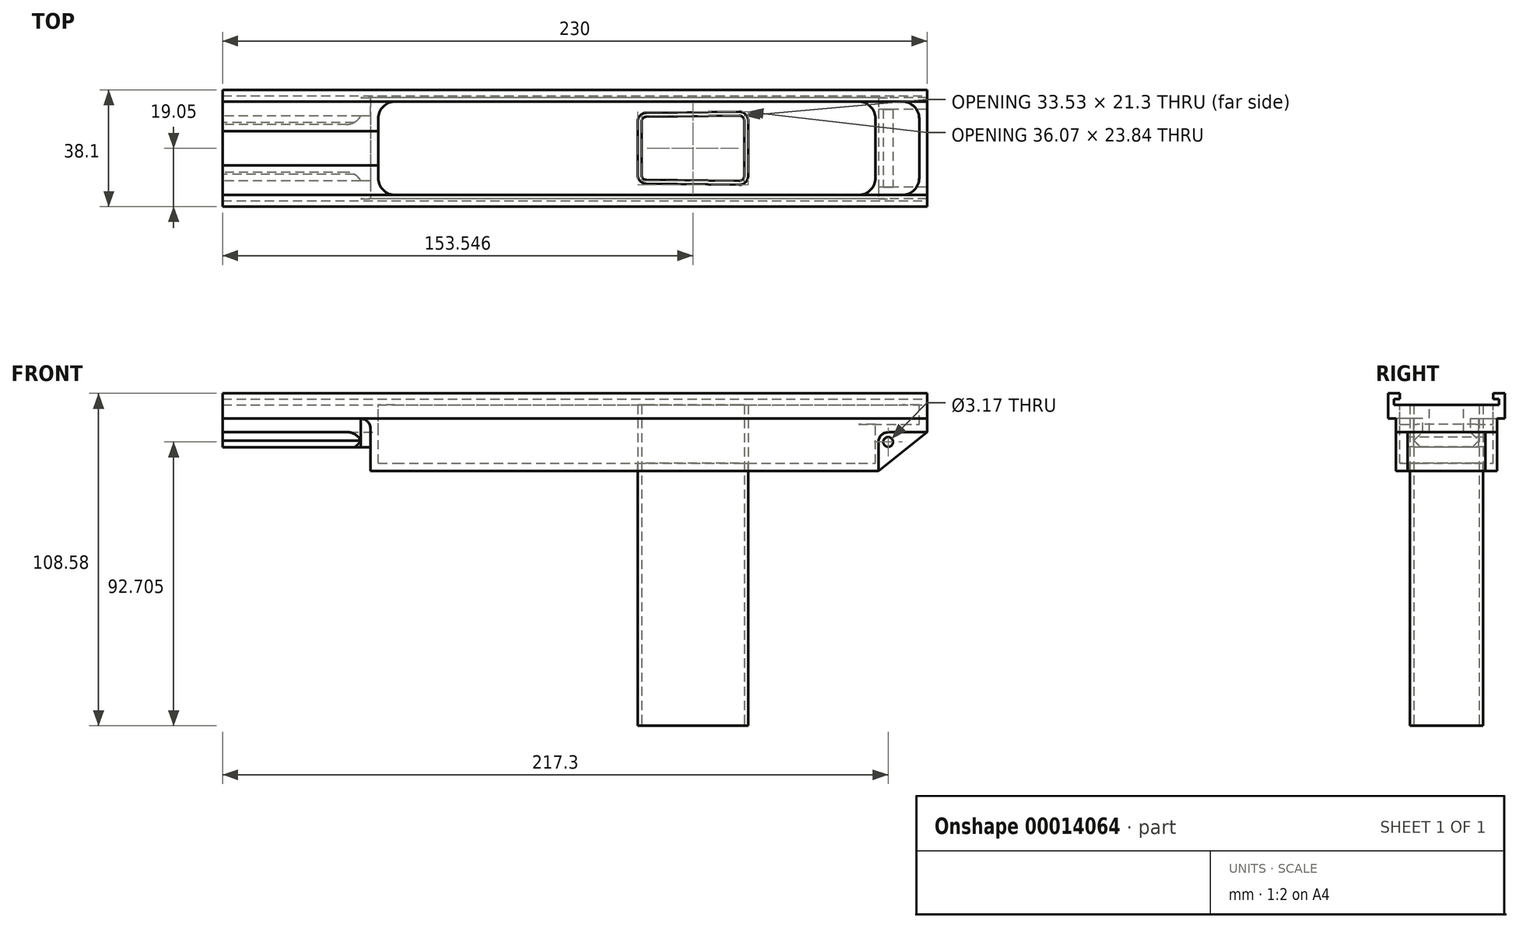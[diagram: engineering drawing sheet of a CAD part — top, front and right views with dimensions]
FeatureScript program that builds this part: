
annotation { "Feature Type Name" : "Feature", "Feature Type Description" : "" }
export const myFeature = defineFeature(function(context is Context, id is Id, definition is map)
    precondition{}
    {
        {
            var Q0;
            Q0=qCreatedBy(makeId("Top.planeOp"),FACE);
            var sketch = newSketch(context, id + "F0", { "sketchPlane" : qUnion([Q0])});
            skLineSegment(sketch, "E0.rect.bottom", {"start": v(-115, 19.05) * mm, "end": v(115, 19.05) * mm});
            skLineSegment(sketch, "E0.rect.top", {"start": v(-115, -19.05) * mm, "end": v(115, -19.05) * mm});
            skLineSegment(sketch, "E0.rect.left", {"start": v(-115, 19.05) * mm, "end": v(-115, -19.05) * mm});
            skLineSegment(sketch, "E0.rect.right", {"start": v(115, 19.05) * mm, "end": v(115, -19.05) * mm});
            skPoint(sketch, "E0.rect.middle", {"position": v(0, 0) * mm});
            skSolve(sketch);
        }
        {
            var Q0;
            Q0=makeQuery(id+"F0.imprint","IMPRINT",FACE,{"disambiguationData":[TD([[makeQuery(id+"F0.imprint","IMPRINT",EDGE,{"derivedFrom":sQuery(id+"F0.wireOp",EDGE,"E0.rect.bottom")}),-1.0]])]});
            extrude(context, id + "F1", {"entities" : qUnion([Q0]), "depth" : 25.4 * mm});
        }
        {
            var Q0;
            Q0=makeQuery(id+"F1.opExtrude","CAP_FACE",FACE,{"disambiguationData":[OSD([sQuery(id+"F0.wireOp",EDGE,"E0.rect.bottom"),sQuery(id+"F0.wireOp",EDGE,"E0.rect.top"),sQuery(id+"F0.wireOp",EDGE,"E0.rect.left"),sQuery(id+"F0.wireOp",EDGE,"E0.rect.right")])],"isStart":false});
            var sketch = newSketch(context, id + "F2", { "sketchPlane" : qUnion([Q0])});
            skLineSegment(sketch, "E1.rect.bottom", {"start": v(-115, 15.24) * mm, "end": v(112.46, 15.24) * mm});
            skLineSegment(sketch, "E1.rect.top", {"start": v(-115, -15.24) * mm, "end": v(112.46, -15.24) * mm});
            skLineSegment(sketch, "E1.rect.left", {"start": v(-115, 15.24) * mm, "end": v(-115, -15.24) * mm});
            skLineSegment(sketch, "E1.rect.right", {"start": v(112.46, 15.24) * mm, "end": v(112.46, -15.24) * mm});
            skPoint(sketch, "E1.rect.middle", {"position": v(0, 0) * mm});
            skLineSegment(sketch, "E2", {"start": v(112.46, 15.24) * mm, "end": v(112.46, 19.05) * mm, "construction": true});
            skLineSegment(sketch, "E3", {"start": v(112.46, -15.24) * mm, "end": v(112.46, -19.05) * mm, "construction": true});
            skLineSegment(sketch, "E4", {"start": v(-64.2, 15.24) * mm, "end": v(-64.2, -15.24) * mm});
            skLineSegment(sketch, "E5.bottom", {"start": v(-115, 5.56) * mm, "end": v(-64.2, 5.56) * mm});
            skLineSegment(sketch, "E5.top", {"start": v(-115, -5.56) * mm, "end": v(-64.2, -5.56) * mm});
            skLineSegment(sketch, "E5.left", {"start": v(-115, 5.56) * mm, "end": v(-115, -5.56) * mm});
            skLineSegment(sketch, "E5.right", {"start": v(-64.2, 5.56) * mm, "end": v(-64.2, -5.56) * mm});
            skLineSegment(sketch, "E6", {"start": v(-115, 15.24) * mm, "end": v(-64.2, 5.56) * mm, "construction": true});
            skLineSegment(sketch, "E7", {"start": v(-115, -15.24) * mm, "end": v(-64.2, -5.56) * mm, "construction": true});
            skSolve(sketch);
        }
        {
            var Q0;
            {var subQ1=sQuery(id+"F2.wireOp",EDGE,"E1.rect.right");Q0=makeQuery(id+"F2.imprint","IMPRINT",FACE,{"disambiguationData":[TD([[makeQuery(id+"F2.imprint","IMPRINT",EDGE,{"derivedFrom":subQ1}),-1.0]])]});}
            extrude(context, id + "F3", {"entities" : qUnion([Q0]), "operationType" : NewBodyOperationType.REMOVE, "oppositeDirection" : true, "depth" : 10.16 * mm});
        }
        {
            var Q0;
            Q0=makeQuery(id+"F3.boolean.opBoolean","COPY",FACE,{"derivedFrom":makeQuery(id+"F3.opExtrude","CAP_FACE",FACE,{"disambiguationData":[OSD([sQuery(id+"F2.wireOp",EDGE,"E1.rect.bottom"),sQuery(id+"F2.wireOp",EDGE,"E1.rect.top"),sQuery(id+"F2.wireOp",EDGE,"E1.rect.left"),sQuery(id+"F2.wireOp",EDGE,"E1.rect.right")])],"isStart":false})});
            var sketch = newSketch(context, id + "F4", { "sketchPlane" : qUnion([Q0])});
            skLineSegment(sketch, "E8.bottom", {"start": v(98.17, 15.24) * mm, "end": v(112.46, 15.24) * mm});
            skLineSegment(sketch, "E8.top", {"start": v(98.17, -15.24) * mm, "end": v(112.46, -15.24) * mm});
            skLineSegment(sketch, "E8.left", {"start": v(112.46, 15.24) * mm, "end": v(112.46, -15.24) * mm});
            skLineSegment(sketch, "E8.right", {"start": v(98.17, 15.24) * mm, "end": v(98.17, -15.24) * mm});
            skLineSegment(sketch, "E9.0", {"start": v(-64.2, 15.24) * mm, "end": v(-64.2, -15.24) * mm});
            skLineSegment(sketch, "E10.bottom", {"start": v(-64.2, 15.24) * mm, "end": v(98.17, 15.24) * mm});
            skLineSegment(sketch, "E10.top", {"start": v(-64.2, -15.24) * mm, "end": v(98.17, -15.24) * mm});
            skSolve(sketch);
        }
        {
            var Q0;
            Q0=makeQuery(id+"F2.imprint","IMPRINT",FACE,{"disambiguationData":[TD([[makeQuery(id+"F2.imprint","IMPRINT",EDGE,{"derivedFrom":sQuery(id+"F2.wireOp",EDGE,"E5.bottom")}),-1.0]])]});
            extrude(context, id + "F5", {"entities" : qUnion([Q0]), "operationType" : NewBodyOperationType.REMOVE, "oppositeDirection" : true, "depth" : 12.7 * mm});
        }
        {
            var Q0;
            Q0=makeQuery(id+"F4.imprint","IMPRINT",FACE,{"disambiguationData":[TD([[makeQuery(id+"F4.imprint","IMPRINT",EDGE,{"derivedFrom":sQuery(id+"F4.wireOp",EDGE,"E10.bottom")}),-1.0]])]});
            extrude(context, id + "F6", {"entities" : qUnion([Q0]), "operationType" : NewBodyOperationType.REMOVE, "oppositeDirection" : true, "depth" : 12.7 * mm});
        }
        {
            var Q0;
            Q0=makeQuery(id+"F3.boolean.opBoolean","COPY",EDGE,{"derivedFrom":makeQuery(id+"F3.opExtrude","SWEPT_EDGE",EDGE,{"disambiguationData":[OSD([sQuery(id+"F2.wireOp",EDGE,"E1.rect.bottom"),sQuery(id+"F2.wireOp",EDGE,"E1.rect.right")])]})});
            var Q1;
            Q1=makeQuery(id+"F3.boolean.opBoolean","COPY",EDGE,{"derivedFrom":makeQuery(id+"F3.opExtrude","SWEPT_EDGE",EDGE,{"disambiguationData":[OSD([sQuery(id+"F2.wireOp",EDGE,"E1.rect.top"),sQuery(id+"F2.wireOp",EDGE,"E1.rect.right")])]})});
            var Q2;
            Q2=makeQuery(id+"F6.boolean.opBoolean","COPY",EDGE,{"derivedFrom":makeQuery(id+"F6.opExtrude","SWEPT_EDGE",EDGE,{"disambiguationData":[OSD([sQuery(id+"F4.wireOp",EDGE,"E8.bottom"),sQuery(id+"F4.wireOp",EDGE,"E10.bottom"),sQuery(id+"F4.wireOp",EDGE,"E8.right")])]})});
            var Q3;
            Q3=makeQuery(id+"F6.boolean.opBoolean","COPY",EDGE,{"derivedFrom":makeQuery(id+"F6.opExtrude","SWEPT_EDGE",EDGE,{"disambiguationData":[OSD([sQuery(id+"F4.wireOp",EDGE,"E8.top"),sQuery(id+"F4.wireOp",EDGE,"E10.top"),sQuery(id+"F4.wireOp",EDGE,"E8.right")])]})});
            var Q4;
            Q4=makeQuery(id+"F6.boolean.opBoolean","MERGE",EDGE,{"derivedFrom":[makeQuery(id+"F3.boolean.opBoolean","COPY",EDGE,{"derivedFrom":makeQuery(id+"F3.opExtrude","SWEPT_EDGE",EDGE,{"disambiguationData":[OSD([sQuery(id+"F2.wireOp",EDGE,"E1.rect.bottom"),sQuery(id+"F2.wireOp",EDGE,"E4")])]})}),makeQuery(id+"F6.opExtrude","SWEPT_EDGE",EDGE,{"disambiguationData":[OSD([sQuery(id+"F4.wireOp",EDGE,"E10.bottom"),sQuery(id+"F4.wireOp",EDGE,"E9.0")])]})]});
            var Q5;
            Q5=makeQuery(id+"F6.boolean.opBoolean","MERGE",EDGE,{"derivedFrom":[makeQuery(id+"F3.boolean.opBoolean","COPY",EDGE,{"derivedFrom":makeQuery(id+"F3.opExtrude","SWEPT_EDGE",EDGE,{"disambiguationData":[OSD([sQuery(id+"F2.wireOp",EDGE,"E1.rect.top"),sQuery(id+"F2.wireOp",EDGE,"E4")])]})}),makeQuery(id+"F6.opExtrude","SWEPT_EDGE",EDGE,{"disambiguationData":[OSD([sQuery(id+"F4.wireOp",EDGE,"E10.top"),sQuery(id+"F4.wireOp",EDGE,"E9.0")])]})]});
            fillet(context, id + "F7", {"entities" : qUnion([Q0, Q1, Q2, Q3, Q4, Q5]), "radius" : 5.56 * mm, "tangentPropagation" : true, "allowEdgeOverflow" : false});
        }
        {
            var Q0;
            Q0=makeQuery(id+"F1.opExtrude","SWEPT_FACE",FACE,{"disambiguationData":[OSD([sQuery(id+"F0.wireOp",EDGE,"E0.rect.top")])]});
            var sketch = newSketch(context, id + "F8", { "sketchPlane" : qUnion([Q0])});
            skLineSegment(sketch, "E11.bottom", {"start": v(115, 0) * mm, "end": v(99.12, 0) * mm});
            skLineSegment(sketch, "E11.top", {"start": v(115, 12.7) * mm, "end": v(102.3, 12.7) * mm});
            skLineSegment(sketch, "E11.left", {"start": v(115, 0) * mm, "end": v(115, 12.7) * mm});
            skLineSegment(sketch, "E11.right", {"start": v(99.12, 0) * mm, "end": v(99.12, 9.52) * mm});
            skLineSegment(sketch, "E12.bottom", {"start": v(-115, 0) * mm, "end": v(-70.3, 0) * mm});
            skLineSegment(sketch, "E12.top", {"start": v(-115, 13.39) * mm, "end": v(-70.3, 13.39) * mm});
            skLineSegment(sketch, "E12.left", {"start": v(-115, 0) * mm, "end": v(-115, 13.39) * mm});
            skLineSegment(sketch, "E12.right", {"start": v(-70.3, 0) * mm, "end": v(-70.3, 13.39) * mm});
            skLineSegment(sketch, "E13", {"start": v(115, 12.7) * mm, "end": v(99.12, 0) * mm});
            skPoint(sketch, "E14.visualSharp", {"position": v(99.12, 12.7) * mm});
            skArc(sketch, "E14.filletArc", {"start": v(102.3, 12.7) * mm, "mid": v(100.05, 11.77) * mm, "end": v(99.12, 9.52) * mm});
            skCircle(sketch, "E15", {"center": v(102.3, 9.52) * mm, "radius": 1.59 * mm});
            skSolve(sketch);
        }
        {
            var Q0;
            Q0=makeQuery(id+"F8.imprint","IMPRINT",FACE,{"disambiguationData":[TD([[makeQuery(id+"F8.imprint","IMPRINT",EDGE,{"derivedFrom":sQuery(id+"F8.wireOp",EDGE,"E11.bottom")}),1.0]])]});
            var Q1;
            Q1=makeQuery(id+"F8.imprint","IMPRINT",FACE,{"disambiguationData":[TD([[makeQuery(id+"F8.imprint","IMPRINT",EDGE,{"derivedFrom":sQuery(id+"F8.wireOp",EDGE,"E15")}),1.0]])]});
            extrude(context, id + "F9", {"entities" : qUnion([Q0, Q1]), "operationType" : NewBodyOperationType.REMOVE, "endBound" : BoundingType.THROUGH_ALL, "oppositeDirection" : true, "depth" : 25.4 * mm});
        }
        {
            var Q0;
            Q0=makeQuery(id+"F8.imprint","IMPRINT",FACE,{"disambiguationData":[TD([[makeQuery(id+"F8.imprint","IMPRINT",EDGE,{"derivedFrom":sQuery(id+"F8.wireOp",EDGE,"E11.top")}),1.0]])]});
            extrude(context, id + "F10", {"entities" : qUnion([Q0]), "operationType" : NewBodyOperationType.REMOVE, "oppositeDirection" : true, "depth" : 6.35 * mm, "hasSecondDirection" : true, "secondDirectionOppositeDirection" : false, "secondDirectionDepth" : 25.4 * mm});
        }
        {
            var Q0;
            Q0=makeQuery(id+"F8.imprint","IMPRINT",FACE,{"disambiguationData":[TD([[makeQuery(id+"F8.imprint","IMPRINT",EDGE,{"derivedFrom":sQuery(id+"F8.wireOp",EDGE,"E11.top")}),1.0]])]});
            extrude(context, id + "F11", {"entities" : qUnion([Q0]), "operationType" : NewBodyOperationType.REMOVE, "oppositeDirection" : true, "depth" : 38.1 * mm, "hasSecondDirection" : true, "secondDirectionOppositeDirection" : true, "secondDirectionDepth" : 31.75 * mm});
        }
        {
            var Q0;
            Q0=makeQuery(id+"F1.opExtrude","SWEPT_FACE",FACE,{"disambiguationData":[OSD([sQuery(id+"F0.wireOp",EDGE,"E0.rect.right")])]});
            var sketch = newSketch(context, id + "F12", { "sketchPlane" : qUnion([Q0])});
            skLineSegment(sketch, "E16.0", {"start": v(15.24, 15.24) * mm, "end": v(-15.24, 15.24) * mm});
            skLineSegment(sketch, "E17.bottom", {"start": v(-15.24, 15.24) * mm, "end": v(15.24, 15.24) * mm, "construction": true});
            skLineSegment(sketch, "E17.top", {"start": v(-15.24, 25.4) * mm, "end": v(15.24, 25.4) * mm, "construction": true});
            skLineSegment(sketch, "E17.left", {"start": v(-15.24, 15.24) * mm, "end": v(-15.24, 25.4) * mm, "construction": true});
            skLineSegment(sketch, "E17.right", {"start": v(15.24, 15.24) * mm, "end": v(15.24, 25.4) * mm, "construction": true});
            skLineSegment(sketch, "E18.bottom", {"start": v(-15.24, 25.4) * mm, "end": v(15.24, 25.4) * mm});
            skLineSegment(sketch, "E18.left", {"start": v(-15.24, 25.4) * mm, "end": v(-15.24, 23.5) * mm});
            skLineSegment(sketch, "E18.right", {"start": v(15.24, 25.4) * mm, "end": v(15.24, 23.5) * mm});
            skLineSegment(sketch, "E19.bottom", {"start": v(-17.14, 23.5) * mm, "end": v(-15.24, 23.5) * mm});
            skLineSegment(sketch, "E19.top", {"start": v(-17.14, 21.6) * mm, "end": v(17.14, 21.6) * mm});
            skLineSegment(sketch, "E19.left", {"start": v(-17.14, 23.5) * mm, "end": v(-17.14, 21.6) * mm});
            skLineSegment(sketch, "E19.right", {"start": v(17.14, 23.5) * mm, "end": v(17.14, 21.6) * mm});
            skLineSegment(sketch, "E20.trimOffspring", {"start": v(15.24, 23.5) * mm, "end": v(17.14, 23.5) * mm});
            skSolve(sketch);
        }
        {
            var Q0;
            Q0=makeQuery(id+"F12.imprint","IMPRINT",FACE,{"disambiguationData":[TD([[makeQuery(id+"F12.imprint","IMPRINT",EDGE,{"derivedFrom":sQuery(id+"F12.wireOp",EDGE,"E18.bottom")}),1.0]])]});
            var Q1;
            Q1=makeQuery(id+"F12.imprint","IMPRINT",FACE,{"disambiguationData":[TD([[makeQuery(id+"F12.imprint","IMPRINT",EDGE,{"derivedFrom":sQuery(id+"F12.wireOp",EDGE,"E19.top")}),1.0]])]});
            extrude(context, id + "F13", {"entities" : qUnion([Q0, Q1]), "operationType" : NewBodyOperationType.REMOVE, "endBound" : BoundingType.THROUGH_ALL, "oppositeDirection" : true, "depth" : 25.4 * mm});
        }
        {
            var Q0;
            Q0=makeQuery(id+"F6.boolean.opBoolean","COPY",FACE,{"derivedFrom":makeQuery(id+"F6.opExtrude","CAP_FACE",FACE,{"disambiguationData":[OSD([sQuery(id+"F4.wireOp",EDGE,"E10.bottom"),sQuery(id+"F4.wireOp",EDGE,"E10.top"),sQuery(id+"F4.wireOp",EDGE,"E9.0"),sQuery(id+"F4.wireOp",EDGE,"E8.right")])],"isStart":false})});
            var sketch = newSketch(context, id + "F14", { "sketchPlane" : qUnion([Q0])});
            skLineSegment(sketch, "E21.0", {"start": v(115, -17.14) * mm, "end": v(115, 17.14) * mm});
            skLineSegment(sketch, "E22.bottom", {"start": v(115, 17.14) * mm, "end": v(56.58, 17.14) * mm, "construction": true});
            skLineSegment(sketch, "E22.top", {"start": v(115, -17.14) * mm, "end": v(56.58, -17.14) * mm, "construction": true});
            skLineSegment(sketch, "E22.left", {"start": v(115, 17.14) * mm, "end": v(115, -17.14) * mm, "construction": true});
            skLineSegment(sketch, "E22.right", {"start": v(56.58, 17.14) * mm, "end": v(56.58, -17.14) * mm, "construction": true});
            skLineSegment(sketch, "E23", {"start": v(0, 0) * mm, "end": v(56.58, 0) * mm, "construction": true});
            skLineSegment(sketch, "E24", {"start": v(21.78, -8.72) * mm, "end": v(21.78, 8.72) * mm});
            skLineSegment(sketch, "E25", {"start": v(55.31, 9.06) * mm, "end": v(55.31, -9.06) * mm});
            skLineSegment(sketch, "E26", {"start": v(23.35, 10.3) * mm, "end": v(53.7, 10.65) * mm});
            skLineSegment(sketch, "E27", {"start": v(21.78, 0) * mm, "end": v(55.31, 0) * mm, "construction": true});
            skLineSegment(sketch, "E28", {"start": v(53.7, -10.65) * mm, "end": v(23.35, -10.3) * mm});
            skPoint(sketch, "E29.visualSharp", {"position": v(21.78, 10.29) * mm});
            skLineSegment(sketch, "E30.1", {"start": v(23.34, 11.57) * mm, "end": v(53.7, 11.92) * mm});
            skLineSegment(sketch, "E30.3", {"start": v(20.51, -8.72) * mm, "end": v(20.51, 8.72) * mm});
            skPoint(sketch, "E31.visualSharp", {"position": v(55.3, 10.67) * mm});
            skPoint(sketch, "E32.visualSharp", {"position": v(21.78, -10.29) * mm});
            skPoint(sketch, "E33.visualSharp", {"position": v(55.31, -10.67) * mm});
            skLineSegment(sketch, "E30.5", {"start": v(56.58, 9.06) * mm, "end": v(56.58, -9.06) * mm});
            skLineSegment(sketch, "E30.6", {"start": v(53.7, -11.92) * mm, "end": v(23.34, -11.57) * mm});
            skArc(sketch, "E30.4", {"start": v(20.51, -8.72) * mm, "mid": v(21.34, -10.73) * mm, "end": v(23.34, -11.57) * mm});
            skArc(sketch, "E30.7", {"start": v(53.7, -11.92) * mm, "mid": v(55.73, -11.1) * mm, "end": v(56.58, -9.06) * mm});
            skArc(sketch, "E29.filletArc", {"start": v(23.35, 10.3) * mm, "mid": v(22.24, 9.83) * mm, "end": v(21.78, 8.72) * mm});
            skArc(sketch, "E32.filletArc", {"start": v(21.78, -8.72) * mm, "mid": v(22.24, -9.83) * mm, "end": v(23.35, -10.3) * mm});
            skArc(sketch, "E33.filletArc", {"start": v(53.7, -10.65) * mm, "mid": v(54.84, -10.2) * mm, "end": v(55.31, -9.06) * mm});
            skArc(sketch, "E31.filletArc", {"start": v(55.31, 9.06) * mm, "mid": v(54.84, 10.2) * mm, "end": v(53.7, 10.65) * mm});
            skArc(sketch, "E30.0", {"start": v(56.58, 9.06) * mm, "mid": v(55.73, 11.1) * mm, "end": v(53.7, 11.92) * mm});
            skArc(sketch, "E30.2", {"start": v(23.34, 11.57) * mm, "mid": v(21.34, 10.73) * mm, "end": v(20.51, 8.72) * mm});
            skSolve(sketch);
        }
        {
            var Q0;
            Q0=makeQuery(id+"F14.imprint","IMPRINT",FACE,{"disambiguationData":[TD([[makeQuery(id+"F14.imprint","IMPRINT",EDGE,{"derivedFrom":sQuery(id+"F14.wireOp",EDGE,"E24")}),1.0]])]});
            var Q1;
            Q1=makeQuery(id+"F14.imprint","IMPRINT",FACE,{"disambiguationData":[TD([[makeQuery(id+"F14.imprint","IMPRINT",EDGE,{"derivedFrom":sQuery(id+"F14.wireOp",EDGE,"E24")}),-1.0]])]});
            extrude(context, id + "F15", {"entities" : qUnion([Q0, Q1]), "operationType" : NewBodyOperationType.REMOVE, "endBound" : BoundingType.THROUGH_ALL, "oppositeDirection" : true, "depth" : 25.4 * mm});
        }
        {
            var Q0;
            Q0=makeQuery(id+"F14.imprint","IMPRINT",FACE,{"disambiguationData":[TD([[makeQuery(id+"F14.imprint","IMPRINT",EDGE,{"derivedFrom":sQuery(id+"F14.wireOp",EDGE,"E24")}),1.0]])]});
            extrude(context, id + "F16", {"entities" : qUnion([Q0]), "depth" : 19.05 * mm, "hasSecondDirection" : true, "secondDirectionOppositeDirection" : true, "secondDirectionDepth" : 85.72 * mm});
        }
        {
            var Q0;
            Q0=makeQuery(id+"F1.opExtrude","SWEPT_FACE",FACE,{"disambiguationData":[OSD([sQuery(id+"F0.wireOp",EDGE,"E0.rect.left")])]});
            var sketch = newSketch(context, id + "F17", { "sketchPlane" : qUnion([Q0])});
            skLineSegment(sketch, "E34", {"start": v(-7.8, 17.14) * mm, "end": v(-7.8, 12.79) * mm});
            skLineSegment(sketch, "E35", {"start": v(-7.8, 12.79) * mm, "end": v(-10.6, 9.98) * mm});
            skLineSegment(sketch, "E36", {"start": v(-10.6, 9.98) * mm, "end": v(-8.45, 7.82) * mm});
            skLineSegment(sketch, "E37", {"start": v(-8.45, 7.82) * mm, "end": v(8.45, 7.82) * mm});
            skLineSegment(sketch, "E38", {"start": v(8.45, 7.82) * mm, "end": v(10.6, 9.98) * mm});
            skLineSegment(sketch, "E39", {"start": v(10.6, 9.98) * mm, "end": v(7.8, 12.79) * mm});
            skLineSegment(sketch, "E40", {"start": v(7.8, 12.79) * mm, "end": v(7.8, 17.14) * mm});
            skLineSegment(sketch, "E41", {"start": v(-9.53, 8.9) * mm, "end": v(9.52, 8.9) * mm, "construction": true});
            skLineSegment(sketch, "E42", {"start": v(-7.8, 17.14) * mm, "end": v(7.8, 17.14) * mm, "construction": true});
            skLineSegment(sketch, "E43", {"start": v(-7.8, 17.14) * mm, "end": v(-19.05, 17.14) * mm});
            skLineSegment(sketch, "E44", {"start": v(-19.05, 17.15) * mm, "end": v(-19.05, 7.82) * mm});
            skLineSegment(sketch, "E45", {"start": v(-19.05, 7.82) * mm, "end": v(-8.45, 7.82) * mm});
            skLineSegment(sketch, "E46", {"start": v(7.8, 17.14) * mm, "end": v(19.05, 17.14) * mm});
            skLineSegment(sketch, "E47", {"start": v(19.05, 17.14) * mm, "end": v(19.05, 7.82) * mm});
            skLineSegment(sketch, "E48", {"start": v(19.05, 7.82) * mm, "end": v(8.45, 7.82) * mm});
            skLineSegment(sketch, "E49", {"start": v(-19.05, 17.15) * mm, "end": v(-7.8, 12.79) * mm, "construction": true});
            skLineSegment(sketch, "E50", {"start": v(7.8, 12.79) * mm, "end": v(19.05, 17.14) * mm, "construction": true});
            skLineSegment(sketch, "E51", {"start": v(16.5, 17.14) * mm, "end": v(16.5, 0) * mm});
            skLineSegment(sketch, "E52", {"start": v(-16.51, 17.14) * mm, "end": v(-16.51, 0) * mm});
            skLineSegment(sketch, "E53", {"start": v(-16.51, 17.14) * mm, "end": v(-19.05, 7.82) * mm, "construction": true});
            skLineSegment(sketch, "E54", {"start": v(16.5, 17.14) * mm, "end": v(19.05, 7.82) * mm, "construction": true});
            skLineSegment(sketch, "E55", {"start": v(10.6, 7.82) * mm, "end": v(10.6, 9.98) * mm});
            skLineSegment(sketch, "E56", {"start": v(10.6, 9.98) * mm, "end": v(10.6, 17.14) * mm});
            skLineSegment(sketch, "E57", {"start": v(-10.6, 7.82) * mm, "end": v(-10.6, 9.98) * mm});
            skLineSegment(sketch, "E58", {"start": v(-10.6, 9.98) * mm, "end": v(-10.6, 17.14) * mm});
            skLineSegment(sketch, "E59", {"start": v(-7.8, 12.79) * mm, "end": v(-7.8, 7.82) * mm});
            skLineSegment(sketch, "E60", {"start": v(7.8, 12.79) * mm, "end": v(7.8, 7.82) * mm});
            skSolve(sketch);
        }
        {
            var Q0;
            {var subQ1=sQuery(id+"F17.wireOp",EDGE,"E57");Q0=makeQuery(id+"F17.imprint","IMPRINT",FACE,{"disambiguationData":[TD([[makeQuery(id+"F17.imprint","IMPRINT",EDGE,{"derivedFrom":subQ1}),1.0]])]});}
            var Q1;
            {var subQ1=sQuery(id+"F17.wireOp",EDGE,"E55");Q1=makeQuery(id+"F17.imprint","IMPRINT",FACE,{"disambiguationData":[TD([[makeQuery(id+"F17.imprint","IMPRINT",EDGE,{"derivedFrom":subQ1}),-1.0]])]});}
            var Q2;
            {var subQ10=sQuery(id+"F17.wireOp",EDGE,"E37");Q2=makeQuery(id+"F17.imprint","IMPRINT",FACE,{"disambiguationData":[TD([[makeQuery(id+"F17.imprint","IMPRINT",EDGE,{"derivedFrom":subQ10}),-1.0]])]});}
            extrude(context, id + "F18", {"entities" : qUnion([Q0, Q1, Q2]), "operationType" : NewBodyOperationType.REMOVE, "oppositeDirection" : true, "depth" : 48.26 * mm});
        }
        {
            var Q0;
            {var subQ6=sQuery(id+"F17.wireOp",EDGE,"E44");Q0=makeQuery(id+"F17.imprint","IMPRINT",FACE,{"disambiguationData":[TD([[makeQuery(id+"F17.imprint","IMPRINT",EDGE,{"derivedFrom":subQ6}),1.0]])]});}
            var Q1;
            {var subQ0=sQuery(id+"F0.wireOp",EDGE,"E0.rect.left");var subQ4=makeQuery(id+"F1.opExtrude","CAP_EDGE",EDGE,{"disambiguationData":[OSD([subQ0])],"isStart":true});var subQ6=sQuery(id+"F17.wireOp",EDGE,"E52");var subQ7=makeQuery(id+"F17.imprint","INTERSECT",VERTEX,{"derivedFrom":[subQ4,subQ6]});Q1=makeQuery(id+"F17.imprint","IMPRINT",FACE,{"disambiguationData":[TD([[makeQuery(id+"F17.imprint","IMPRINT",EDGE,{"disambiguationData":[TD([[subQ7,1.0]])],"derivedFrom":subQ6}),-1.0]])]});}
            var Q2;
            {var subQ6=sQuery(id+"F17.wireOp",EDGE,"E47");Q2=makeQuery(id+"F17.imprint","IMPRINT",FACE,{"disambiguationData":[TD([[makeQuery(id+"F17.imprint","IMPRINT",EDGE,{"derivedFrom":subQ6}),-1.0]])]});}
            var Q3;
            {var subQ0=sQuery(id+"F0.wireOp",EDGE,"E0.rect.left");var subQ1=makeQuery(id+"F1.opExtrude","CAP_EDGE",EDGE,{"disambiguationData":[OSD([subQ0])],"isStart":true});var subQ2=sQuery(id+"F17.wireOp",EDGE,"E51");var subQ3=makeQuery(id+"F17.imprint","INTERSECT",VERTEX,{"derivedFrom":[subQ1,subQ2]});Q3=makeQuery(id+"F17.imprint","IMPRINT",FACE,{"disambiguationData":[TD([[makeQuery(id+"F17.imprint","IMPRINT",EDGE,{"disambiguationData":[TD([[subQ3,1.0]])],"derivedFrom":subQ2}),1.0]])]});}
            extrude(context, id + "F19", {"entities" : qUnion([Q0, Q1, Q2, Q3]), "operationType" : NewBodyOperationType.REMOVE, "endBound" : BoundingType.THROUGH_ALL, "oppositeDirection" : true, "depth" : 25.4 * mm});
        }
        {
            var Q0;
            Q0=makeQuery(id+"F17.imprint","IMPRINT",FACE,{"disambiguationData":[TD([[makeQuery(id+"F17.imprint","IMPRINT",EDGE,{"derivedFrom":sQuery(id+"F17.wireOp",EDGE,"E39")}),-1.0]])]});
            var Q1;
            {var subQ2=sQuery(id+"F17.wireOp",EDGE,"E38");Q1=makeQuery(id+"F17.imprint","IMPRINT",FACE,{"disambiguationData":[TD([[makeQuery(id+"F17.imprint","IMPRINT",EDGE,{"derivedFrom":subQ2}),-1.0]])]});}
            var Q2;
            {var subQ2=sQuery(id+"F17.wireOp",EDGE,"E36");Q2=makeQuery(id+"F17.imprint","IMPRINT",FACE,{"disambiguationData":[TD([[makeQuery(id+"F17.imprint","IMPRINT",EDGE,{"derivedFrom":subQ2}),-1.0]])]});}
            var Q3;
            {var subQ2=sQuery(id+"F17.wireOp",EDGE,"E34");Q3=makeQuery(id+"F17.imprint","IMPRINT",FACE,{"disambiguationData":[TD([[makeQuery(id+"F17.imprint","IMPRINT",EDGE,{"derivedFrom":subQ2}),-1.0]])]});}
            var Q4;
            Q4=makeQuery(id+"F17.imprint","IMPRINT",FACE,{"disambiguationData":[TD([[makeQuery(id+"F17.imprint","IMPRINT",EDGE,{"derivedFrom":sQuery(id+"F17.wireOp",EDGE,"E35")}),1.0]])]});
            var Q5;
            {var subQ1=sQuery(id+"F17.wireOp",EDGE,"E38");Q5=makeQuery(id+"F17.imprint","IMPRINT",FACE,{"disambiguationData":[TD([[makeQuery(id+"F17.imprint","IMPRINT",EDGE,{"derivedFrom":subQ1}),1.0]])]});}
            extrude(context, id + "F20", {"entities" : qUnion([Q0, Q1, Q2, Q3, Q4, Q5]), "operationType" : NewBodyOperationType.REMOVE, "oppositeDirection" : true, "depth" : 45.08 * mm});
        }
        {
            var Q0;
            Q0=makeQuery(id+"F20.boolean.opBoolean","COPY",EDGE,{"derivedFrom":makeQuery(id+"F20.opExtrude","CAP_EDGE",EDGE,{"disambiguationData":[OSD([sQuery(id+"F17.wireOp",EDGE,"E34"),sQuery(id+"F17.wireOp",EDGE,"E59")])],"isStart":false})});
            var Q1;
            Q1=makeQuery(id+"F20.boolean.opBoolean","COPY",EDGE,{"derivedFrom":makeQuery(id+"F20.opExtrude","CAP_EDGE",EDGE,{"disambiguationData":[OSD([sQuery(id+"F17.wireOp",EDGE,"E40"),sQuery(id+"F17.wireOp",EDGE,"E60")])],"isStart":false})});
            fillet(context, id + "F21", {"entities" : qUnion([Q0, Q1]), "radius" : 5.08 * mm, "tangentPropagation" : true, "allowEdgeOverflow" : false});
        }
        {
            var Q0;
            Q0=makeQuery(id+"F17.imprint","IMPRINT",FACE,{"disambiguationData":[TD([[makeQuery(id+"F17.imprint","IMPRINT",EDGE,{"derivedFrom":sQuery(id+"F17.wireOp",EDGE,"E35")}),1.0]])]});
            var Q1;
            {var subQ1=sQuery(id+"F17.wireOp",EDGE,"E38");Q1=makeQuery(id+"F17.imprint","IMPRINT",FACE,{"disambiguationData":[TD([[makeQuery(id+"F17.imprint","IMPRINT",EDGE,{"derivedFrom":subQ1}),1.0]])]});}
            var Q2;
            Q2=makeQuery(id+"F18.boolean.opBoolean","COPY",FACE,{"derivedFrom":makeQuery(id+"F18.opExtrude","CAP_FACE",FACE,{"disambiguationData":[OSD([sQuery(id+"F0.wireOp",EDGE,"E0.rect.left"),sQuery(id+"F17.wireOp",EDGE,"E37"),sQuery(id+"F17.wireOp",EDGE,"E43"),sQuery(id+"F17.wireOp",EDGE,"E45"),sQuery(id+"F17.wireOp",EDGE,"E46"),sQuery(id+"F17.wireOp",EDGE,"E48"),sQuery(id+"F17.wireOp",EDGE,"E51"),sQuery(id+"F17.wireOp",EDGE,"E52"),sQuery(id+"F17.wireOp",EDGE,"E55"),sQuery(id+"F17.wireOp",EDGE,"E56"),sQuery(id+"F17.wireOp",EDGE,"E57"),sQuery(id+"F17.wireOp",EDGE,"E58")])],"isStart":false})});
            extrude(context, id + "F22", {"entities" : qUnion([Q0, Q1]), "operationType" : NewBodyOperationType.ADD, "endBound" : BoundingType.UP_TO_SURFACE, "oppositeDirection" : true, "endBoundEntityFace" : qUnion([Q2]), "depth" : 25.4 * mm});
        }
        {
            var Q0;
            Q0=makeQuery(id+"F18.boolean.opBoolean","COPY",EDGE,{"derivedFrom":makeQuery(id+"F18.opExtrude","CAP_EDGE",EDGE,{"disambiguationData":[OSD([sQuery(id+"F17.wireOp",EDGE,"E46")])],"isStart":false})});
            var Q1;
            Q1=makeQuery(id+"F18.boolean.opBoolean","COPY",EDGE,{"derivedFrom":makeQuery(id+"F18.opExtrude","CAP_EDGE",EDGE,{"disambiguationData":[OSD([sQuery(id+"F17.wireOp",EDGE,"E43")])],"isStart":false})});
            fillet(context, id + "F23", {"entities" : qUnion([Q0, Q1]), "radius" : 3.17 * mm, "tangentPropagation" : true, "allowEdgeOverflow" : false});
        }
    });
